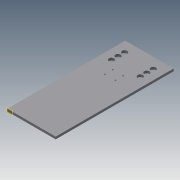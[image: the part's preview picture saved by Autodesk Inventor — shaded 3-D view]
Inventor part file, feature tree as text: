
AUTODESK INVENTOR PART (.ipt)
format: ipt  version: 2014 SP1 (Build 180222100, 222)  size: 115,712 bytes
history: native  units: in
note: dims shown in document units (in); Inventor stores cm internally (conversion verified against a paired STEP export)
features: extrude x2, sketch x2, plane x1
ambient origin geometry x8: Origin, YZ Plane, XZ Plane, XY Plane, X Axis, Y Axis, Z Axis, Center Point
bodies: Solid1 (feature_tree)
feature tree (5):
  plane  "Work Plane1"
  extrude  "Extrusion1"  Depth=11.2726in TaperAngle=0.0deg
  extrude  "Extrusion2"  Depth=0.2228in
  sketch  "Sketch1"  dims[d0=0.2228in d2=11.2726in d3=0.0in]
  sketch  "Sketch2"  dims[d4=1.0in d5=0.75in d6=3.0in d7=0.5in d8=0.125in d9=0.125in d10=0.125in d11=0.125in d12=0.5in d13=0.5in d14=0.625in d15=1.0in d16=0.5in d17=0.625in d18=0.5in d19=0.5in d20=0.5in d21=0.625in d22=0.625in d23=1.0in d24=1.375in d25=1.375in d26=0.2228in d27=0.0in]
